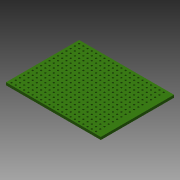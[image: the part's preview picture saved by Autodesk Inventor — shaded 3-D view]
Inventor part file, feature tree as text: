
AUTODESK INVENTOR PART (.ipt)
format: ipt  version: 2014 (Build 180170000, 170)  size: 361,984 bytes
history: native  units: in
note: dims shown in document units (in); Inventor stores cm internally (conversion verified against a paired STEP export)
features: extrude x2, sketch x2, pattern_linear x1
ambient origin geometry x8: Origin, YZ Plane, XZ Plane, XY Plane, X Axis, Y Axis, Z Axis, Center Point
bodies: Solid1 (feature_tree)
feature tree (5):
  extrude  "Extrusion1"  Depth=1.7323in
  extrude  "Extrusion2"  Depth=0.062in
  pattern_linear  "Rectangular Pattern1"  Spacing1=0.075in  [1 undecoded]
  sketch  "Sketch1"  dims[d0=2.2441in d1=1.7323in]
  sketch  "Sketch2"  dims[d2=0.062in d3=0.0in d4=0.041in d5=0.075in d6=0.075in d7=0.062in d8=0.0in d9=8.2677in d11=0.1in d12=6.6929in d14=0.1in]
note: 1 required parameter value undecoded (feature->parameter linkage not recoverable at this tier; creation-order binding heuristic only, values carry confidence <= 0.55)
